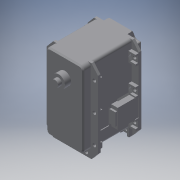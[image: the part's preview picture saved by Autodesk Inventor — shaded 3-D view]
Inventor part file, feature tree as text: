
AUTODESK INVENTOR PART (.ipt)
format: ipt  version: 2016 (Build 200138000, 138)  size: 516,608 bytes
history: native  units: in
note: dims shown in document units (in); Inventor stores cm internally (conversion verified against a paired STEP export)
features: other x3, sketch x1
ambient origin geometry x8: Origin, YZ Plane, XZ Plane, XY Plane, X Axis, Y Axis, Z Axis, Center Point
bodies: Solid1 (feature_tree)
feature tree (4):
  other  "MX-106T.ipt"
  other  "Solid1::MX-106T.ipt"
  other  "TaggingFeature1"
  sketch  "Sketch1"  dims[d0=0.3937in]
